# Revit family: MODE045045060B00
name_source: partatom
category: Specialty Equipment
revit_build: Autodesk Revit 2018 (Build: 22.0.11200.0000)
units: mm (PartAtom-declared; Revit-internal decimal feet)

## family parameters
Always vertical = Yes
Cut with Voids When Loaded = No
OmniClass Number = 23.60.30.17
OmniClass Title = Manholes
Part Type = Normal
Room Calculation Point = No
Round Connector Dimension = Use Diameter
Shared = No
Work Plane-Based = No

## types (1)
- Standard
    Connector_10_Diameter = 0 mm  [stored 0 ft]
    Connector_1_Diameter = 0 mm  [stored 0 ft]
    Connector_2_Diameter = 0 mm  [stored 0 ft]
    Connector_7_Diameter = 0 mm  [stored 0 ft]
    Connector_8_Diameter = 0 mm  [stored 0 ft]
    Connector_9_Diameter = 0 mm  [stored 0 ft]
    Description = MODE045045060B00
    Manufacturer = PowerCast
    Model = EVput 450x450x600
    URL = https://evput.nl

note: [stored X ft] marks values corroborated as IEEE doubles in the binary element streams (Revit-internal decimal feet)

## geometry (parser evidence)
native form markers: Sweep x2
no freeform markers — native parametric forms only
